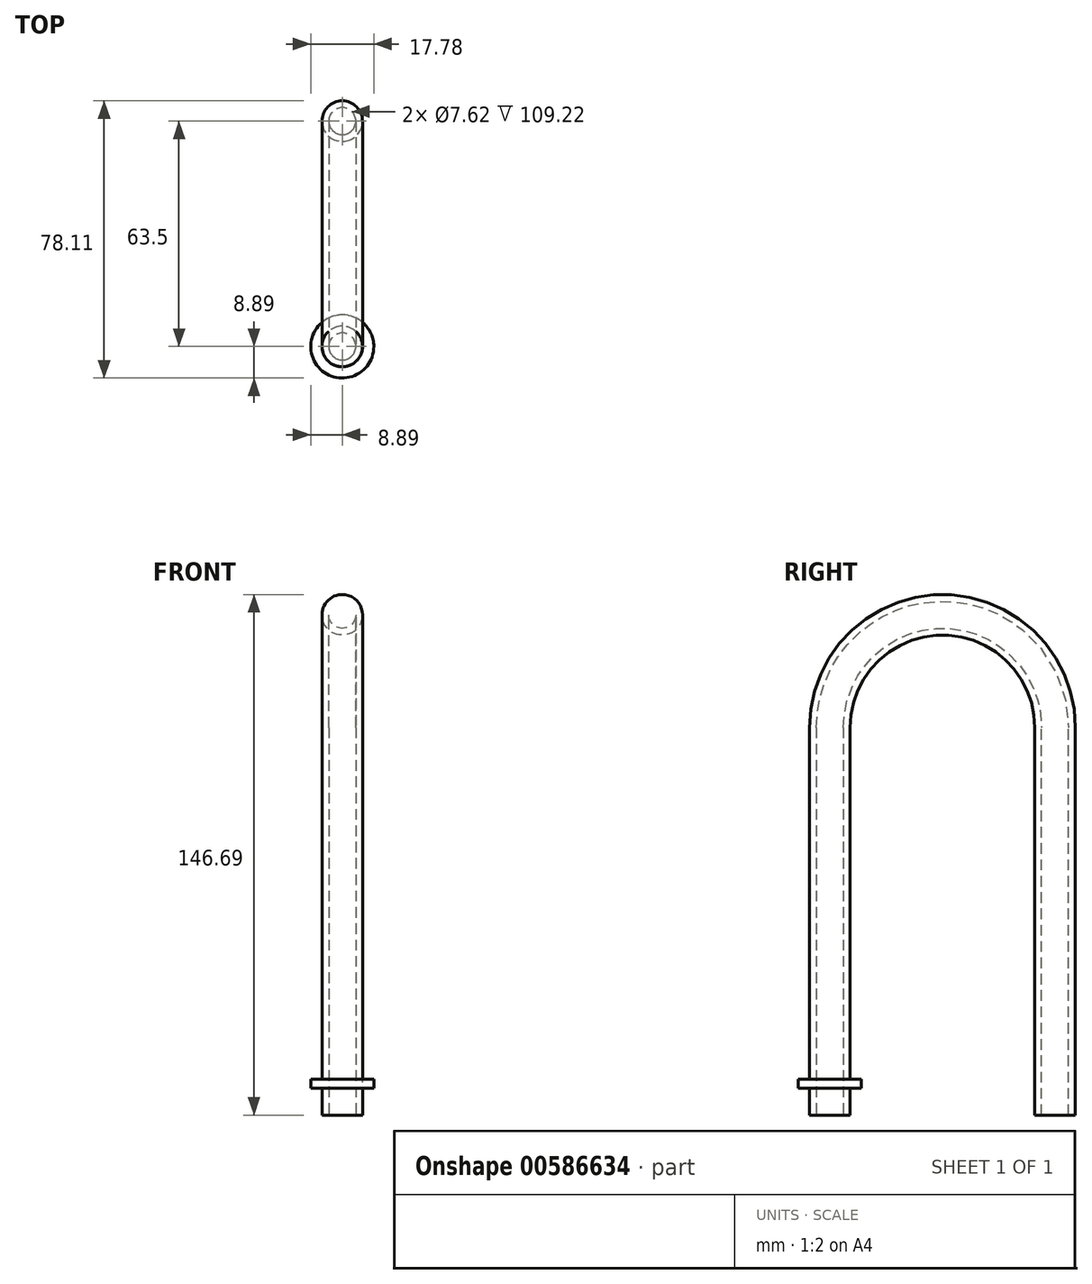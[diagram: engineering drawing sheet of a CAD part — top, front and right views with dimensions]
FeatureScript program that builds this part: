
annotation { "Feature Type Name" : "Feature", "Feature Type Description" : "" }
export const myFeature = defineFeature(function(context is Context, id is Id, definition is map)
    precondition{}
    {
        {
            var Q0;
            Q0=qCreatedBy(makeId("Right.planeOp"),FACE);
            var sketch = newSketch(context, id + "F0", { "sketchPlane" : qUnion([Q0])});
            skArc(sketch, "E0", {"start": v(31.75, 0) * mm, "mid": v(0, 31.75) * mm, "end": v(-31.75, 0) * mm});
            skLineSegment(sketch, "E1", {"start": v(-31.75, 0) * mm, "end": v(-31.75, -109.22) * mm});
            skLineSegment(sketch, "E2", {"start": v(31.75, 0) * mm, "end": v(31.75, -109.22) * mm});
            skSolve(sketch);
        }
        {
            var Q0;
            Q0=qCreatedBy(makeId("Top.planeOp"),FACE);
            var sketch = newSketch(context, id + "F1", { "sketchPlane" : qUnion([Q0])});
            skCircle(sketch, "E3", {"center": v(0, -31.75) * mm, "radius": 3.81 * mm});
            skCircle(sketch, "E4", {"center": v(0, -31.75) * mm, "radius": 5.72 * mm});
            skSolve(sketch);
        }
        {
            var Q0;
            Q0=makeQuery(id+"F1.imprint","IMPRINT",FACE,{"disambiguationData":[TD([[makeQuery(id+"F1.imprint","IMPRINT",EDGE,{"derivedFrom":sQuery(id+"F1.wireOp",EDGE,"E3")}),-1.0]])]});
            var Q1;
            Q1=sQuery(id+"F0.wireOp",EDGE,"E0");
            var Q2;
            Q2=sQuery(id+"F0.wireOp",EDGE,"E1");
            var Q3;
            Q3=sQuery(id+"F0.wireOp",EDGE,"E2");
            sweep(context, id + "F2", {"profiles" : qUnion([Q0]), "path" : qUnion([Q1, Q2, Q3])});
        }
        {
            var Q0;
            Q0=qCreatedBy(makeId("Top.planeOp"),FACE);
            cPlane(context, id + "F3", {"entities" : qUnion([Q0]), "cplaneType" : CPlaneType.OFFSET, "offset" : 101.6 * mm, "oppositeDirection" : true, "width" : 152.4 * mm, "height" : 152.4 * mm});
        }
        {
            var Q0;
            Q0=qCreatedBy(id+"F3.planeOp",FACE);
            var sketch = newSketch(context, id + "F4", { "sketchPlane" : qUnion([Q0])});
            skCircle(sketch, "E5", {"center": v(0, -31.75) * mm, "radius": 8.9 * mm});
            skCircle(sketch, "E6", {"center": v(0, -31.75) * mm, "radius": 4.36 * mm});
            skSolve(sketch);
        }
        {
            var Q0;
            Q0 = qSketchRegion(id + "F4", true);
            extrude(context, id + "F5", {"entities" : qUnion([Q0]), "operationType" : NewBodyOperationType.ADD, "depth" : 2.54 * mm, "offsetDistance" : 25.4 * mm});
        }
    });
